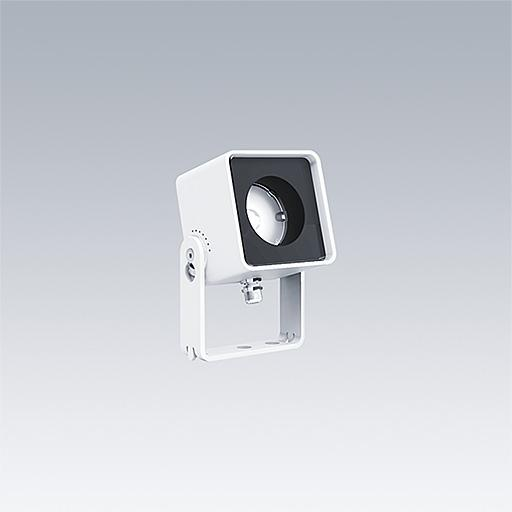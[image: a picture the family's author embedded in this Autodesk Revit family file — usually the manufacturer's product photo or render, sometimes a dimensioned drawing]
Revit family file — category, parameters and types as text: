
# Revit family: Thorn Caelon S3x
name_source: partatom
category: Lighting Fixtures
units: mm (PartAtom-declared; Revit-internal decimal feet)

## family parameters
Cut with Voids When Loaded = No
Host = Face
Light Source = No
Maintain Annotation Orientation = No
Part Type = Normal
Room Calculation Point = No
Round Connector Dimension = Use Diameter
Shared = No

## types (18) — shared parameters
Apparent Load = 20 VA
Assembly Code = Pr_70_70_48_75
Description = Outdoor flood and spotlight luminaires
Export Type to IFC As = IfcLightFixtureType
Lamp = LED
Luminaire Height = 79 mm
Luminaire Length = 38 mm  [stored 0.124672 ft]
Luminaire Width = 56 mm  [stored 0.183727 ft]
Manufacturer = Thorn Lighting
Power Factor = 1
Type Bracket Black = Thorn-Parts-CAELON-Bracket-S3x : Black
Type Bracket White = Thorn-Parts-CAELON-Bracket-S3x : White
Type Housing Black = Thorn-Parts-CAELON-Housing-S3x : Black
Type Housing White = Thorn-Parts-CAELON-Housing-S3x : White
Type IFC Predefined Type = DIRECTIONSOURCE
URL = https://www.thornlighting.com
Wattage = 6 VA
zero-valued in all types: Default Elevation

## per-type parameters (varying)
| type | Housing Finish Black | Housing Finish White | Model | Optic | Type Bracket | Type Housing | Type Image | Type Light Source |
| CAELON S3x 320-827 F BK 2M 66 | Yes | No | 21013585 | Far | Thorn-Parts-CAELON-Bracket-S3x : Black | Thorn-Parts-CAELON-Housing-S3x : Black | TLG_CAEL_F_S3x_BK.jpg | Thorn-Light Sources-CAELON S3x : CAELON S3x 320-827 F BK 2M 66_photometric_data |
| CAELON S3x 320-827 F WH 2M 66 | No | Yes | 21013584 | Far | Thorn-Parts-CAELON-Bracket-S3x : White | Thorn-Parts-CAELON-Housing-S3x : White | TLG_CAEL_F_S3x_WH.jpg | Thorn-Light Sources-CAELON S3x : CAELON S3x 320-827 F WH 2M 66_photometric_data |
| CAELON S3x 320-827 M BK 2M 66 | Yes | No | 21013583 | Medium | Thorn-Parts-CAELON-Bracket-S3x : Black | Thorn-Parts-CAELON-Housing-S3x : Black | TLG_CAEL_F_S3x_BK.jpg | Thorn-Light Sources-CAELON S3x : CAELON S3x 320-827 M BK 2M 66_photometric_data |
| CAELON S3x 320-827 M WH 2M 66 | No | Yes | 21013582 | Medium | Thorn-Parts-CAELON-Bracket-S3x : White | Thorn-Parts-CAELON-Housing-S3x : White | TLG_CAEL_F_S3x_WH.jpg | Thorn-Light Sources-CAELON S3x : CAELON S3x 320-827 M WH 2M 66_photometric_data |
| CAELON S3x 320-827 N BK 2M 66 | Yes | No | 21013581 | Narrow | Thorn-Parts-CAELON-Bracket-S3x : Black | Thorn-Parts-CAELON-Housing-S3x : Black | TLG_CAEL_F_S3x_BK.jpg | Thorn-Light Sources-CAELON S3x : CAELON S3x 320-827 N BK 2M 66_photometric_data |
| CAELON S3x 320-827 N WH 2M 66 | No | Yes | 21013580 | Narrow | Thorn-Parts-CAELON-Bracket-S3x : White | Thorn-Parts-CAELON-Housing-S3x : White | TLG_CAEL_F_S3x_WH.jpg | Thorn-Light Sources-CAELON S3x : CAELON S3x 320-827 N WH 2M 66_photometric_data |
| CAELON S3x 320-830 F BK 2M 66 | Yes | No | 21013595 | Far | Thorn-Parts-CAELON-Bracket-S3x : Black | Thorn-Parts-CAELON-Housing-S3x : Black | TLG_CAEL_F_S3x_BK.jpg | Thorn-Light Sources-CAELON S3x : CAELON S3x 320-830 F BK 2M 66_photometric_data |
| CAELON S3x 320-830 F WH 2M 66 | No | Yes | 21013594 | Far | Thorn-Parts-CAELON-Bracket-S3x : White | Thorn-Parts-CAELON-Housing-S3x : White | TLG_CAEL_F_S3x_WH.jpg | Thorn-Light Sources-CAELON S3x : CAELON S3x 320-830 F WH 2M 66_photometric_data |
| CAELON S3x 320-830 M BK 2M 66 | Yes | No | 21013593 | Medium | Thorn-Parts-CAELON-Bracket-S3x : Black | Thorn-Parts-CAELON-Housing-S3x : Black | TLG_CAEL_F_S3x_BK.jpg | Thorn-Light Sources-CAELON S3x : CAELON S3x 320-830 M BK 2M 66_photometric_data |
| CAELON S3x 320-830 M WH 2M 66 | No | Yes | 21013592 | Medium | Thorn-Parts-CAELON-Bracket-S3x : White | Thorn-Parts-CAELON-Housing-S3x : White | TLG_CAEL_F_S3x_WH.jpg | Thorn-Light Sources-CAELON S3x : CAELON S3x 320-830 M WH 2M 66_photometric_data |
| CAELON S3x 320-830 N BK 2M 66 | Yes | No | 21013591 | Narrow | Thorn-Parts-CAELON-Bracket-S3x : Black | Thorn-Parts-CAELON-Housing-S3x : Black | TLG_CAEL_F_S3x_BK.jpg | Thorn-Light Sources-CAELON S3x : CAELON S3x 320-830 N BK 2M 66_photometric_data |
| CAELON S3x 320-830 N WH 2M 66 | No | Yes | 21013590 | Narrow | Thorn-Parts-CAELON-Bracket-S3x : White | Thorn-Parts-CAELON-Housing-S3x : White | TLG_CAEL_F_S3x_WH.jpg | Thorn-Light Sources-CAELON S3x : CAELON S3x 320-830 N WH 2M 66_photometric_data |
| CAELON S3x 320-840 F BK 2M 66 | Yes | No | 21013605 | Far | Thorn-Parts-CAELON-Bracket-S3x : Black | Thorn-Parts-CAELON-Housing-S3x : Black | TLG_CAEL_F_S3x_BK.jpg | Thorn-Light Sources-CAELON S3x : CAELON S3x 320-840 F BK 2M 66_photometric_data |
| CAELON S3x 320-840 F WH 2M 66 | No | Yes | 21013604 | Far | Thorn-Parts-CAELON-Bracket-S3x : White | Thorn-Parts-CAELON-Housing-S3x : White | TLG_CAEL_F_S3x_WH.jpg | Thorn-Light Sources-CAELON S3x : CAELON S3x 320-840 F WH 2M 66_photometric_data |
| CAELON S3x 320-840 M BK 2M 66 | Yes | No | 21013603 | Medium | Thorn-Parts-CAELON-Bracket-S3x : Black | Thorn-Parts-CAELON-Housing-S3x : Black | TLG_CAEL_F_S3x_BK.jpg | Thorn-Light Sources-CAELON S3x : CAELON S3x 320-840 M BK 2M 66_photometric_data |
| CAELON S3x 320-840 M WH 2M 66 | No | Yes | 21013602 | Medium | Thorn-Parts-CAELON-Bracket-S3x : White | Thorn-Parts-CAELON-Housing-S3x : White | TLG_CAEL_F_S3x_WH.jpg | Thorn-Light Sources-CAELON S3x : CAELON S3x 320-840 M WH 2M 66_photometric_data |
| CAELON S3x 320-840 N BK 2M 66 | Yes | No | 21013601 | Narrow | Thorn-Parts-CAELON-Bracket-S3x : Black | Thorn-Parts-CAELON-Housing-S3x : Black | TLG_CAEL_F_S3x_BK.jpg | Thorn-Light Sources-CAELON S3x : CAELON S3x 320-840 N BK 2M 66_photometric_data |
| CAELON S3x 320-840 N WH 2M 66 | No | Yes | 21013600 | Narrow | Thorn-Parts-CAELON-Bracket-S3x : White | Thorn-Parts-CAELON-Housing-S3x : White | TLG_CAEL_F_S3x_WH.jpg | Thorn-Light Sources-CAELON S3x : CAELON S3x 320-840 N WH 2M 66_photometric_data |

note: [stored X ft] marks values corroborated as IEEE doubles in the binary element streams (Revit-internal decimal feet)

## geometry (parser evidence)
native form markers: Sweep x9
no freeform markers — native parametric forms only
